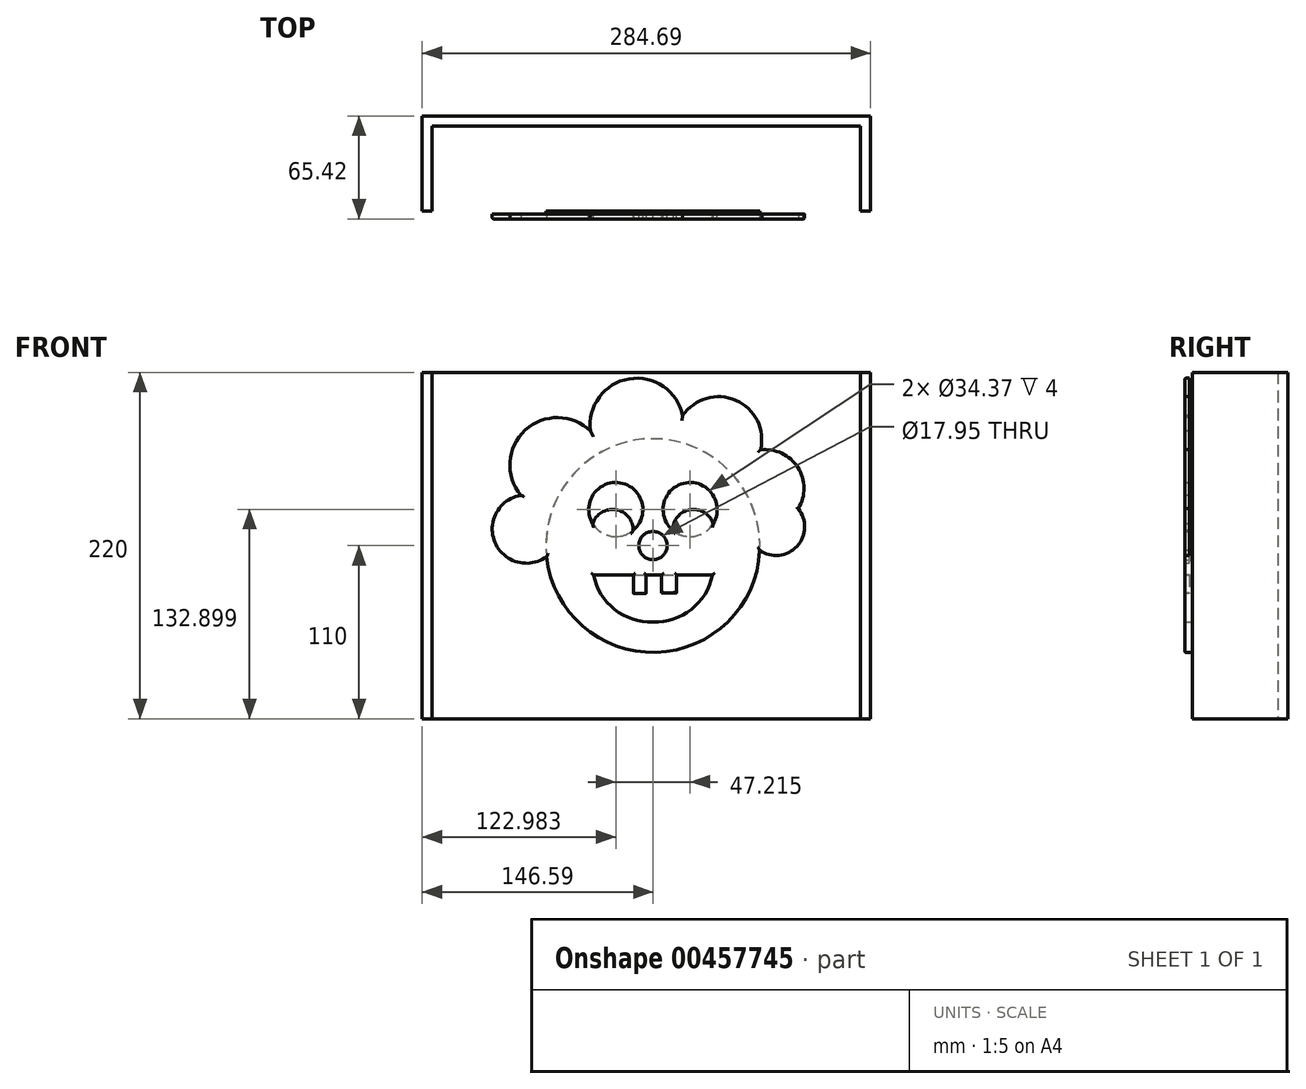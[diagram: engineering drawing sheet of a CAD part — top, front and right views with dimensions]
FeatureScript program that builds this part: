
annotation { "Feature Type Name" : "Feature", "Feature Type Description" : "" }
export const myFeature = defineFeature(function(context is Context, id is Id, definition is map)
    precondition{}
    {
        {
            var Q0;
            Q0=qCreatedBy(makeId("Front.planeOp"),FACE);
            var sketch = newSketch(context, id + "F0", { "sketchPlane" : qUnion([Q0])});
            skCircle(sketch, "E0", {"center": v(0, 0) * mm, "radius": 67.86 * mm});
            skSolve(sketch);
        }
        {
            var Q0;
            Q0 = qSketchRegion(id + "F0", true);
            extrude(context, id + "F1", {"entities" : qUnion([Q0]), "depth" : 5 * mm});
        }
        {
            var Q0;
            Q0=makeQuery(id+"F0.imprint","IMPRINT",FACE,{"disambiguationData":[TD([[makeQuery(id+"F0.imprint","IMPRINT",EDGE,{"derivedFrom":sQuery(id+"F0.wireOp",EDGE,"E0")}),1.0]])]});
            var sketch = newSketch(context, id + "F2", { "sketchPlane" : qUnion([Q0])});
            skCircle(sketch, "E1", {"center": v(-23.6, 22.9) * mm, "radius": 17.19 * mm});
            skCircle(sketch, "E2.MirrorC", {"center": v(23.6, 22.9) * mm, "radius": 17.19 * mm});
            skArc(sketch, "E3", {"start": v(0, -48.4) * mm, "mid": v(24.36, -40.47) * mm, "end": v(37.77, -18.65) * mm});
            skArc(sketch, "E4.MirrorCS", {"start": v(0, -48.4) * mm, "mid": v(-24.36, -40.47) * mm, "end": v(-37.77, -18.65) * mm});
            skLineSegment(sketch, "E5", {"start": v(-37.77, -18.65) * mm, "end": v(37.77, -18.65) * mm});
            skCircle(sketch, "E6", {"center": v(0, 0) * mm, "radius": 8.97 * mm});
            skSolve(sketch);
        }
        {
            var Q0;
            Q0 = qSketchRegion(id + "F2", true);
            extrude(context, id + "F3", {"entities" : qUnion([Q0]), "operationType" : NewBodyOperationType.REMOVE, "depth" : 5 * mm});
        }
        {
            var Q0;
            Q0=makeQuery(id+"F1.opExtrude","CAP_FACE",FACE,{"disambiguationData":[OSD([sQuery(id+"F0.wireOp",EDGE,"E0")])],"isStart":false});
            var sketch = newSketch(context, id + "F4", { "sketchPlane" : qUnion([Q0])});
            skArc(sketch, "E7", {"start": v(-30.88, 55.34) * mm, "mid": v(-83.25, 71.17) * mm, "end": v(-61.31, 21.05) * mm});
            skArc(sketch, "E8", {"start": v(14.98, 60.9) * mm, "mid": v(-13.78, 106.12) * mm, "end": v(-30.88, 55.34) * mm});
            skArc(sketch, "E9", {"start": v(47.13, 40.34) * mm, "mid": v(56.44, 90.3) * mm, "end": v(14.98, 60.9) * mm});
            skArc(sketch, "E10", {"start": v(59.98, 14.62) * mm, "mid": v(93.36, 47.38) * mm, "end": v(47.13, 40.34) * mm});
            skArc(sketch, "E11", {"start": v(-61.31, 21.05) * mm, "mid": v(-102.08, 10.52) * mm, "end": v(-61.31, 0) * mm});
            skArc(sketch, "E12", {"start": v(64.27, 0) * mm, "mid": v(95.61, 17.13) * mm, "end": v(59.98, 14.62) * mm});
            skLineSegment(sketch, "E13", {"start": v(-61.31, 0) * mm, "end": v(-61.31, 21.05) * mm});
            skLineSegment(sketch, "E14", {"start": v(-30.88, 55.34) * mm, "end": v(-61.31, 21.05) * mm});
            skLineSegment(sketch, "E15", {"start": v(-30.88, 55.34) * mm, "end": v(14.98, 60.9) * mm});
            skLineSegment(sketch, "E16", {"start": v(14.98, 60.9) * mm, "end": v(47.13, 40.34) * mm});
            skLineSegment(sketch, "E17", {"start": v(59.98, 14.62) * mm, "end": v(47.13, 40.34) * mm});
            skLineSegment(sketch, "E18", {"start": v(59.98, 14.62) * mm, "end": v(64.27, 0) * mm});
            skLineSegment(sketch, "E19", {"start": v(-12.45, -14.1) * mm, "end": v(-12.45, -30.38) * mm});
            skLineSegment(sketch, "E20", {"start": v(-12.45, -30.38) * mm, "end": v(-4.3, -30.38) * mm});
            skLineSegment(sketch, "E21", {"start": v(-4.3, -30.38) * mm, "end": v(-4.3, -18.65) * mm});
            skLineSegment(sketch, "E22", {"start": v(-4.3, -18.65) * mm, "end": v(5.55, -18.65) * mm});
            skLineSegment(sketch, "E23", {"start": v(5.55, -18.65) * mm, "end": v(5.55, -29.96) * mm});
            skLineSegment(sketch, "E24", {"start": v(5.55, -29.96) * mm, "end": v(14.98, -29.96) * mm});
            skLineSegment(sketch, "E25", {"start": v(14.98, -29.96) * mm, "end": v(14.98, -14.1) * mm});
            skLineSegment(sketch, "E26", {"start": v(14.98, -14.1) * mm, "end": v(-12.45, -14.1) * mm});
            skCircle(sketch, "E27", {"center": v(-25.74, 9.9) * mm, "radius": 13.12 * mm});
            skCircle(sketch, "E28.MirrorC", {"center": v(25.74, 9.9) * mm, "radius": 13.12 * mm});
            skSolve(sketch);
        }
        {
            var Q0;
            Q0 = qSketchRegion(id + "F4", true);
            extrude(context, id + "F5", {"entities" : qUnion([Q0]), "operationType" : NewBodyOperationType.ADD, "oppositeDirection" : true, "depth" : 3 * mm});
        }
        {
            var Q0;
            Q0=makeQuery(id+"F5.boolean.opBoolean","MERGE",FACE,{"derivedFrom":[makeQuery(id+"F1.opExtrude","CAP_FACE",FACE,{"disambiguationData":[OSD([sQuery(id+"F0.wireOp",EDGE,"E0")])],"isStart":false}),makeQuery(id+"F5.opExtrude","CAP_FACE",FACE,{"disambiguationData":[OSD([sQuery(id+"F4.wireOp",EDGE,"E7"),sQuery(id+"F4.wireOp",EDGE,"E8"),sQuery(id+"F4.wireOp",EDGE,"E9"),sQuery(id+"F4.wireOp",EDGE,"E10"),sQuery(id+"F4.wireOp",EDGE,"E11"),sQuery(id+"F4.wireOp",EDGE,"E12"),sQuery(id+"F4.wireOp",EDGE,"E13"),sQuery(id+"F4.wireOp",EDGE,"E14"),sQuery(id+"F4.wireOp",EDGE,"E15"),sQuery(id+"F4.wireOp",EDGE,"E16"),sQuery(id+"F4.wireOp",EDGE,"E17"),sQuery(id+"F4.wireOp",EDGE,"E18")])],"isStart":true}),makeQuery(id+"F5.opExtrude","CAP_FACE",FACE,{"disambiguationData":[OSD([sQuery(id+"F4.wireOp",EDGE,"E19"),sQuery(id+"F4.wireOp",EDGE,"E20"),sQuery(id+"F4.wireOp",EDGE,"E21"),sQuery(id+"F4.wireOp",EDGE,"E22"),sQuery(id+"F4.wireOp",EDGE,"E23"),sQuery(id+"F4.wireOp",EDGE,"E24"),sQuery(id+"F4.wireOp",EDGE,"E25"),sQuery(id+"F4.wireOp",EDGE,"E26")])],"isStart":true}),makeQuery(id+"F5.opExtrude","CAP_FACE",FACE,{"disambiguationData":[OSD([sQuery(id+"F4.wireOp",EDGE,"E27")])],"isStart":true}),makeQuery(id+"F5.opExtrude","CAP_FACE",FACE,{"disambiguationData":[OSD([sQuery(id+"F4.wireOp",EDGE,"E28.MirrorC")])],"isStart":true})]});
            fillet(context, id + "F6", {"entities" : qUnion([Q0]), "radius" : 1 * mm, "tangentPropagation" : true, "allowEdgeOverflow" : false});
        }
        {
            var Q0;
            Q0=qCreatedBy(makeId("Top.planeOp"),FACE);
            var sketch = newSketch(context, id + "F7", { "sketchPlane" : qUnion([Q0])});
            skLineSegment(sketch, "E29", {"start": v(-146.59, 0) * mm, "end": v(-146.59, 60.42) * mm});
            skLineSegment(sketch, "E30", {"start": v(138.1, 60.42) * mm, "end": v(138.1, 0) * mm});
            skLineSegment(sketch, "E31", {"start": v(138.1, 0) * mm, "end": v(138.1, 60.42) * mm});
            skLineSegment(sketch, "E32", {"start": v(138.1, 60.42) * mm, "end": v(-146.59, 60.42) * mm});
            skLineSegment(sketch, "E33.0", {"start": v(-140.24, 0) * mm, "end": v(-140.24, 54.07) * mm});
            skLineSegment(sketch, "E33.1", {"start": v(131.75, 54.07) * mm, "end": v(-140.24, 54.07) * mm});
            skLineSegment(sketch, "E33.2", {"start": v(131.75, 54.07) * mm, "end": v(131.75, 0) * mm});
            skLineSegment(sketch, "E34", {"start": v(-146.59, 0) * mm, "end": v(-140.24, 0) * mm});
            skLineSegment(sketch, "E35", {"start": v(131.75, 0) * mm, "end": v(138.1, 0) * mm});
            skSolve(sketch);
        }
        {
            var Q0;
            Q0 = qSketchRegion(id + "F7", true);
            extrude(context, id + "F8", {"entities" : qUnion([Q0]), "depth" : 220 * mm, "symmetric" : true});
        }
    });
